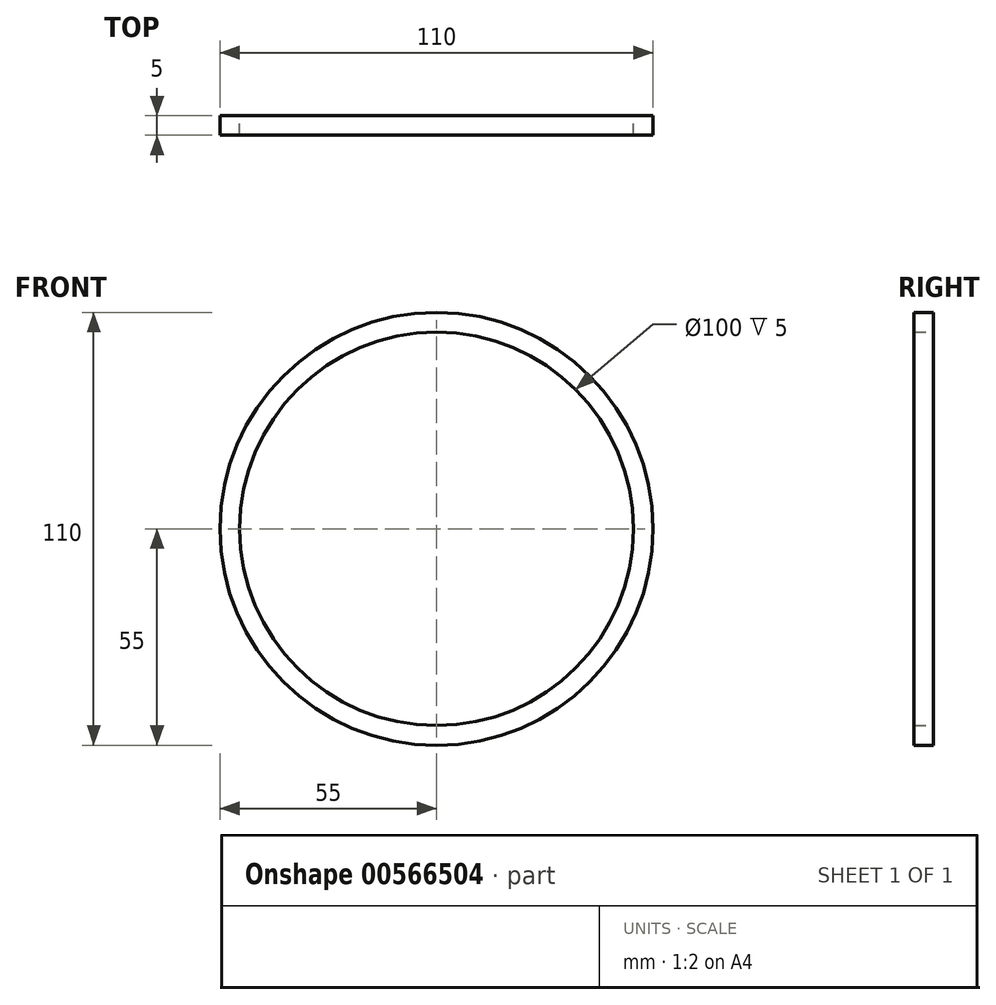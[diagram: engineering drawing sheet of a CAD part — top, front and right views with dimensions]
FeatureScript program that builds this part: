
annotation { "Feature Type Name" : "Feature", "Feature Type Description" : "" }
export const myFeature = defineFeature(function(context is Context, id is Id, definition is map)
    precondition{}
    {
        {
            var Q0;
            Q0=qCreatedBy(makeId("Front.planeOp"),FACE);
            var sketch = newSketch(context, id + "F0", { "sketchPlane" : qUnion([Q0])});
            skCircle(sketch, "E0", {"center": v(0, 0) * mm, "radius": 50 * mm});
            skCircle(sketch, "E1", {"center": v(0, 0) * mm, "radius": 55 * mm});
            skSolve(sketch);
        }
        {
            var Q0;
            Q0=qCreatedBy(makeId("Front.planeOp"),FACE);
            var sketch = newSketch(context, id + "F1", { "sketchPlane" : qUnion([Q0])});
            skSolve(sketch);
        }
        {
            var Q0;
            Q0 = qSketchRegion(id + "F1", true);
            var Q1;
            Q1=makeQuery(id+"F0.imprint","IMPRINT",FACE,{"disambiguationData":[TD([[makeQuery(id+"F0.imprint","IMPRINT",EDGE,{"derivedFrom":sQuery(id+"F0.wireOp",EDGE,"E0")}),-1.0]])]});
            extrude(context, id + "F2", {"entities" : qUnion([Q0, Q1]), "depth" : 5 * mm, "offsetDistance" : 25 * mm});
        }
    });
